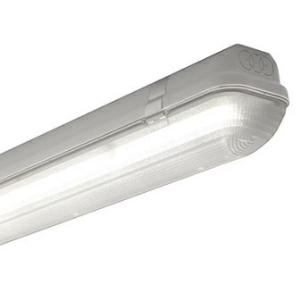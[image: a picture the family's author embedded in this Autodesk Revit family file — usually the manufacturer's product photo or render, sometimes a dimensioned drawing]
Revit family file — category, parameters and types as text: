
# Revit family: 3f_filippi_-_3f_linda_3f_filippi_-_58586_-_3f_linda_led_1x18w_l1270
name_source: partatom
category: Lighting Fixtures
units: mm (PartAtom-declared; Revit-internal decimal feet)

## family parameters
Cut with Voids When Loaded = No
Host = Face
Light Source = No
Part Type = Normal
Room Calculation Point = No
Round Connector Dimension = Use Diameter
Shared = No

## types (1)
- 3F Filippi - 3F Linda (1 x LED, 2967 lm, 20 W, 4000 K)
    Apparent Load = 20 VA
    Approval mark = CE
    CIE Flux Codes = 44 77 94 97 100
    Color Rendering = 80
    Color Temperature = 4000 K
    Control Gear = Electronic ballast
    Default Elevation = 1800 mm
    Description = ILLUMINOTECHNICAL
Luminous efficiency 100% (DLOR 97%, ULOR 3%).
Initial luminous flux of the luminaire 2967 lm.
Controlled symmetric distribution.
Installation Interdistance Transv.D = 1.77 x hu - Long.D = 1.17 x hu.
Tabular UGR (CIE 117 - 4H-8H; S=0.25H; 70/50/20): RUG 20.9 - 21.8.
Beam angle: 109° - 64°.
Luminous efficacy 148 lm/W.
Lifetime (L93/B10): 30000 h. (tq+25°C)
Lifetime (L90/B10): 50000 h. (tq+25°C)
Lifetime (L85/B10): 80000 h. (tq+25°C)
Lifetime (L80/B10): 100000 h. (tq+25°C)
Lifetime (L85/B10): 50000 h. (tq+40°C)
Sudden decreased luminous flux after 50000 hours: 0% (C0).
Photobiological safety in compliance with IEC/TR 62778: RG0 risk exempt, (IEC 62471).
In compliance with IEC/EN 62722-2-1 - IEC/EN 62717 standards.

SOURCE
Linear LED module 18W/840.
Energy efficiency class (UE 2019/2020 - UE 2019/2015): D.
CIE 13.3 Colour rendering index: CRI >80 (R9 <50%).
IES TM-30 Fidelity Index: Rf = 84 Rg = 95.
CCT nominal colour temperature 4000 K.
Colour initial tolerance (MacAdam): SDCM 3.

MECHANICAL
Self-extinguishing V2 polycarbonate housing, injection moulded, RAL 7035 grey.
Ecologic anti-aging injected sealing gasket.
Diffuser in self-extinguishing V2 polycarbonate, photo-engraved interior, UV stabilised, injection moulded with smooth outer surface, tamper-proof opening.
Gear-holder reflector in hot-dip galvanised steel, painted with white polyester base.
Snug fit safety snap-lock clips for diffuser mounting in stainless steel, screwdriver opening.
Fixing brackets in stainless steel.
Possibility for technicians to access the interior of the luminaire.
Luminaire with limited surface temperature. - D - (EN 60598-2-24)
Dimensions: 1270x100 mm, height 100 mm. Weight 2.19 kg.
IP66 protection degree.
Mechanical strength to impacts IK10 (20 joule).
Glow-wire test resistance 850°C.

ELECTRICAL
Halogen Free electronic wiring 230V-50/60Hz, power factor 0.90, THD <25%, constant output current, SELV, class I, 1 driver.
Power of the luminaire 20 W.
ENEC - CE.
SAFE FLICKER: PstLM=<1 and SVM=<0.4 (IEC TR 61547-1 and IEC TR 63158), to ensure a more comfortable and safe light.
Luminaire compliant with EN 60598-2-22 for power supply from a centralised emergency system CPSS (Central Power Supply System), not incorporated in the luminaire - high risk areas excluded. The default power and flux are 100% in AC and 100% in DC.
Ambient temperature from -20°C to +40°C.
Temperature class T6 max 85°C.
Relative humidity UR: <85%.

INSTALLATION
Ceiling / Suspended / Wall.
All accessories dedicated to this product are available on the Catalog and on our website www.3F-Filippi.com.

APPLICATIONS
Suitable product for food production plants (HACCP), IFS (Food Version 6), BRC (GSFS Food Version 7).
Dry, dusty indoor environments, subject to occasional water splashes.
Virtually shatterproof polycarbonate compatibly with the fumes / atmospheres that compromise the elasticity of plastic materials.
Not suitable for installation on surfaces subject to important vibrations, exposed to weather conditions, on ropes or poles.
Suitable for illumination of public car parks and parking grounds referred to DIN 67528:2018-04.

WARNING
Fixture not suitable for cold stores with an ambient temperature <0°C and/or relative humidity >85%.
Luminaire designed for disposal/recycling at end-of-life.
Replaceable (LED only) light source by a professional. Replaceable control gear by a professional.
    Height = 100 mm  [stored 0.328084 ft]
    Lamp = 1 x LED
    Lamp Light Flux = 2967 lm
    Lamp Power = 20 W
    Lamp count = 1
    Length = 1270 mm
    Lifetime = 50000 h
    Luminous efficacy = 148 lm/W
    Manufacturer = 3F Filippi
    ModVariant = No
    Model = 3F Filippi - 58586 - 3F Linda LED 1x18W L1270
    Mounting Place = Ceiling
    Mounting Type = Pendant
    Number of Poles = 1
    OnlyDefault = Yes
    Power Factor = 1
    Product Name = 3F Filippi - 3F Linda
    Product group = pendant luminaire
    ProductGroupID = 9
    Protection Class = Protection class I
    Protection Degree = IP 66
    RLX_Detail_Level = 1
    RLX_Emergency_Light_Flux = 0 lm
    RLX_Emergency_Type = 0
    RLX_Emergency_Type_DB = No
    RlxData = <blob elided: 68705 chars, md5=1ff5c7c1>
    Socket = socket
    Standby Power = 0 W
    System Light Flux = 2967 lm
    System Power = 20 W
    Type Comments = Product without accessories
    Type Image = 3ffilippi_3f_linda_led_1x.jpg
    URL = http://relux.com
    VarID = ---
    Voltage = 0 V
    Weight = 0.00 kg
    Width = 100 mm  [stored 0.328084 ft]

note: [stored X ft] marks values corroborated as IEEE doubles in the binary element streams (Revit-internal decimal feet)

## geometry (parser evidence)
native form markers: Blend x4, Sweep x9
no freeform markers — native parametric forms only
